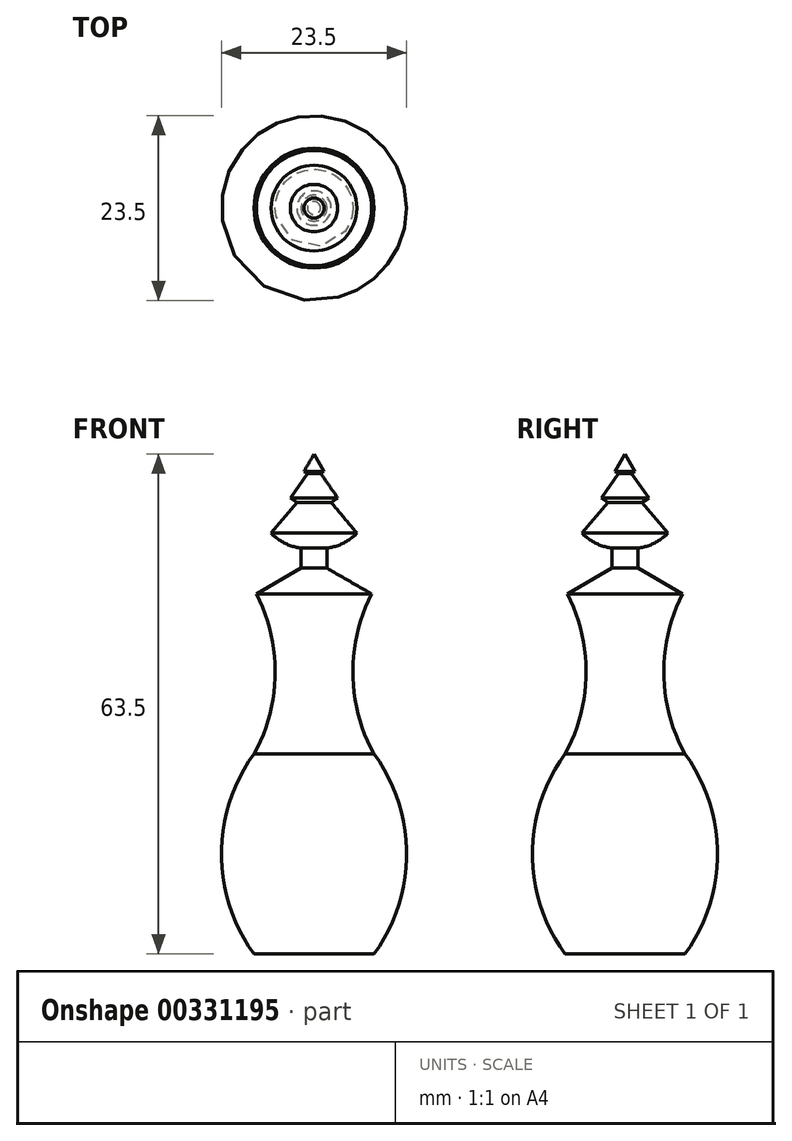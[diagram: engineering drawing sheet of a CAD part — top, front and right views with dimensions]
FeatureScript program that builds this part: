
annotation { "Feature Type Name" : "Feature", "Feature Type Description" : "" }
export const myFeature = defineFeature(function(context is Context, id is Id, definition is map)
    precondition{}
    {
        {
            var Q0;
            Q0=qCreatedBy(makeId("Front.planeOp"),FACE);
            var sketch = newSketch(context, id + "F0", { "sketchPlane" : qUnion([Q0])});
            skLineSegment(sketch, "E0", {"start": v(0, -63.5) * mm, "end": v(-7.62, -63.5) * mm});
            skLineSegment(sketch, "E1.MirrorCS", {"start": v(-1.27, -2.2) * mm, "end": v(-0.83, -2.45) * mm});
            skLineSegment(sketch, "E2.MirrorCS", {"start": v(-3.02, -5.57) * mm, "end": v(-2.18, -6.16) * mm});
            skLineSegment(sketch, "E3.MirrorCS", {"start": v(-1.64, -11.95) * mm, "end": v(-1.64, -14.5) * mm});
            skLineSegment(sketch, "E4.MirrorCS", {"start": v(0, 0) * mm, "end": v(-1.27, -2.2) * mm});
            skLineSegment(sketch, "E5.MirrorCS", {"start": v(-0.83, -2.45) * mm, "end": v(-3.02, -5.57) * mm});
            skLineSegment(sketch, "E6.MirrorCS", {"start": v(-2.18, -6.16) * mm, "end": v(-5.45, -10.05) * mm});
            skArc(sketch, "E7.MirrorCS", {"start": v(-7.33, -17.78) * mm, "mid": v(-4.93, -27.98) * mm, "end": v(-7.62, -38.1) * mm});
            skArc(sketch, "E8.MirrorCS", {"start": v(-7.62, -63.5) * mm, "mid": v(-11.75, -50.8) * mm, "end": v(-7.62, -38.1) * mm});
            skLineSegment(sketch, "E9.MirrorCS", {"start": v(-1.64, -14.5) * mm, "end": v(-7.33, -17.78) * mm});
            skLineSegment(sketch, "E10.MirrorCS", {"start": v(0, 0) * mm, "end": v(0, -63.5) * mm});
            skArc(sketch, "E11.MirrorCS", {"start": v(-1.64, -11.95) * mm, "mid": v(-3.7, -11.33) * mm, "end": v(-5.45, -10.05) * mm});
            skSolve(sketch);
        }
        {
            var Q0;
            Q0=makeQuery(id+"F0.imprint","IMPRINT",FACE,{"disambiguationData":[TD([[makeQuery(id+"F0.imprint","IMPRINT",EDGE,{"derivedFrom":sQuery(id+"F0.wireOp",EDGE,"E0")}),-1.0]])]});
            var Q1;
            Q1=sQuery(id+"F0.wireOp",EDGE,"E10.MirrorCS");
            revolve(context, id + "F1", {"entities" : qUnion([Q0]), "axis" : qUnion([Q1]), "revolveType" : RevolveType.FULL});
        }
    });
